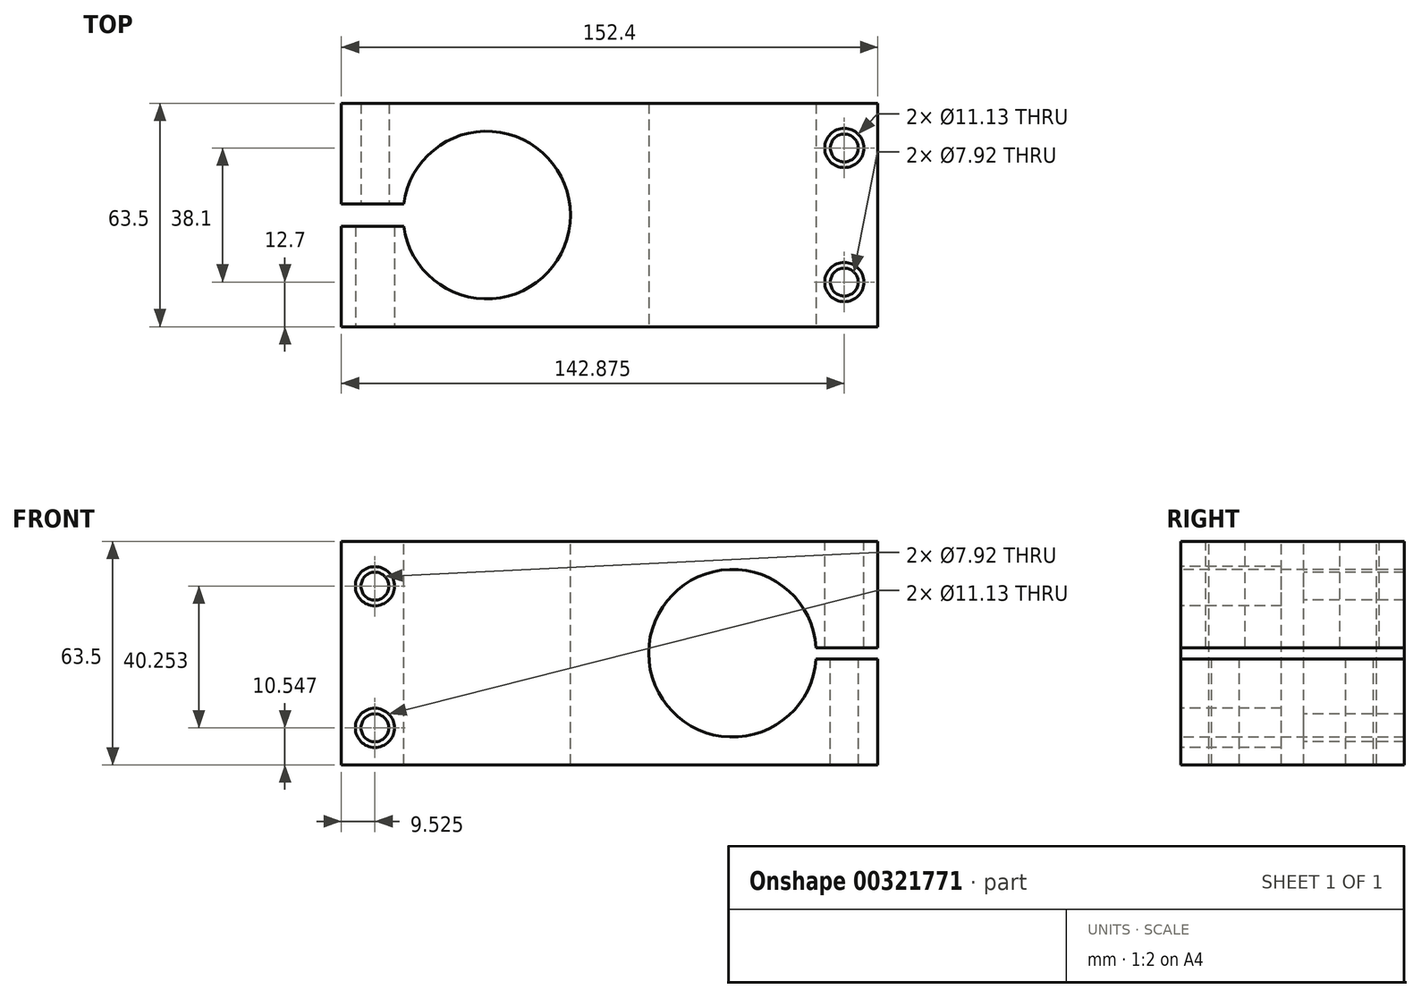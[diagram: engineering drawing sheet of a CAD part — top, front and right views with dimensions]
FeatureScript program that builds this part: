
annotation { "Feature Type Name" : "Feature", "Feature Type Description" : "" }
export const myFeature = defineFeature(function(context is Context, id is Id, definition is map)
    precondition{}
    {
        {
            var Q0;
            Q0=qCreatedBy(makeId("Front.planeOp"),FACE);
            var sketch = newSketch(context, id + "F0", { "sketchPlane" : qUnion([Q0])});
            skLineSegment(sketch, "E0.bottom", {"start": v(-76.2, 31.75) * mm, "end": v(76.2, 31.75) * mm});
            skLineSegment(sketch, "E0.top", {"start": v(-76.2, -31.75) * mm, "end": v(76.2, -31.75) * mm});
            skLineSegment(sketch, "E0.left", {"start": v(-76.2, 31.75) * mm, "end": v(-76.2, -31.75) * mm});
            skLineSegment(sketch, "E0.right", {"start": v(76.2, 31.75) * mm, "end": v(76.2, -31.75) * mm});
            skSolve(sketch);
        }
        {
            var Q0;
            Q0=makeQuery(id+"F0.imprint","IMPRINT",FACE,{"disambiguationData":[TD([[makeQuery(id+"F0.imprint","IMPRINT",EDGE,{"derivedFrom":sQuery(id+"F0.wireOp",EDGE,"E0.bottom")}),-1.0]])]});
            extrude(context, id + "F1", {"entities" : qUnion([Q0]), "endBound" : BoundingType.SYMMETRIC, "depth" : 63.5 * mm});
        }
        {
            var Q0;
            Q0=makeQuery(id+"F1.opExtrude","SWEPT_FACE",FACE,{"disambiguationData":[OSD([sQuery(id+"F0.wireOp",EDGE,"E0.bottom")])]});
            var sketch = newSketch(context, id + "F2", { "sketchPlane" : qUnion([Q0])});
            skPoint(sketch, "E1", {"position": v(-34.92, 0) * mm});
            skSolve(sketch);
        }
        {
            var Q0;
            Q0=sQuery(id+"F2.wireOp",VERTEX,"E1");
            var Q1;
            Q1=makeQuery(id+"F1.opExtrude","SWEPT_BODY",BODY,{"disambiguationData":[OSD([sQuery(id+"F0.wireOp",EDGE,"E0.bottom"),sQuery(id+"F0.wireOp",EDGE,"E0.top"),sQuery(id+"F0.wireOp",EDGE,"E0.left"),sQuery(id+"F0.wireOp",EDGE,"E0.right")])]});
            hole(context, id + "F3", {"style" : HoleStyle.SIMPLE, "endStyle" : HoleEndStyle.THROUGH, "holeDiameter" : 47.62 * mm, "tappedDepth" : 12.7 * mm, "tapClearance" : 3, "locations" : qUnion([Q0]), "scope" : qUnion([Q1])});
        }
        {
            var Q0;
            Q0=makeQuery(id+"F1.opExtrude","CAP_FACE",FACE,{"disambiguationData":[OSD([sQuery(id+"F0.wireOp",EDGE,"E0.bottom"),sQuery(id+"F0.wireOp",EDGE,"E0.top"),sQuery(id+"F0.wireOp",EDGE,"E0.left"),sQuery(id+"F0.wireOp",EDGE,"E0.right")])],"isStart":false});
            var sketch = newSketch(context, id + "F4", { "sketchPlane" : qUnion([Q0])});
            skPoint(sketch, "E2", {"position": v(34.93, 0) * mm});
            skSolve(sketch);
        }
        {
            var Q0;
            Q0=sQuery(id+"F4.wireOp",VERTEX,"E2");
            var Q1;
            Q1=makeQuery(id+"F1.opExtrude","SWEPT_BODY",BODY,{"disambiguationData":[OSD([sQuery(id+"F0.wireOp",EDGE,"E0.bottom"),sQuery(id+"F0.wireOp",EDGE,"E0.top"),sQuery(id+"F0.wireOp",EDGE,"E0.left"),sQuery(id+"F0.wireOp",EDGE,"E0.right")])]});
            hole(context, id + "F5", {"style" : HoleStyle.SIMPLE, "endStyle" : HoleEndStyle.THROUGH, "holeDiameter" : 47.62 * mm, "tappedDepth" : 12.7 * mm, "tapClearance" : 3, "locations" : qUnion([Q0]), "scope" : qUnion([Q1])});
        }
        {
            var Q0;
            Q0=makeQuery(id+"F1.opExtrude","SWEPT_FACE",FACE,{"disambiguationData":[OSD([sQuery(id+"F0.wireOp",EDGE,"E0.bottom")])]});
            var sketch = newSketch(context, id + "F6", { "sketchPlane" : qUnion([Q0])});
            skPoint(sketch, "E3", {"position": v(66.67, 19.05) * mm});
            skSolve(sketch);
        }
        {
            var Q0;
            {var subQ0=sQuery(id+"F0.wireOp",EDGE,"E0.bottom");Q0=makeQuery(id+"F6.imprint","IMPRINT",FACE,{"disambiguationData":[TD([[makeQuery(id+"F6.imprint","IMPRINT",EDGE,{"derivedFrom":makeQuery(id+"F1.opExtrude","CAP_EDGE",EDGE,{"disambiguationData":[OSD([subQ0])],"isStart":true})}),-1.0]])]});}
            var sketch = newSketch(context, id + "F7", { "sketchPlane" : qUnion([Q0])});
            skPoint(sketch, "E4", {"position": v(66.67, -19.05) * mm});
            skSolve(sketch);
        }
        {
            var Q0;
            Q0=makeQuery(id+"F1.opExtrude","CAP_FACE",FACE,{"disambiguationData":[OSD([sQuery(id+"F0.wireOp",EDGE,"E0.bottom"),sQuery(id+"F0.wireOp",EDGE,"E0.top"),sQuery(id+"F0.wireOp",EDGE,"E0.left"),sQuery(id+"F0.wireOp",EDGE,"E0.right")])],"isStart":false});
            var sketch = newSketch(context, id + "F8", { "sketchPlane" : qUnion([Q0])});
            skPoint(sketch, "E5", {"position": v(-66.67, 19.05) * mm});
            skSolve(sketch);
        }
        {
            var Q0;
            Q0=makeQuery(id+"F8.imprint","IMPRINT",FACE,{"disambiguationData":[TD([[makeQuery(id+"F8.imprint","IMPRINT",EDGE,{"derivedFrom":makeQuery(id+"F1.opExtrude","CAP_EDGE",EDGE,{"disambiguationData":[OSD([sQuery(id+"F0.wireOp",EDGE,"E0.bottom")])],"isStart":false})}),-1.0]])]});
            var sketch = newSketch(context, id + "F9", { "sketchPlane" : qUnion([Q0])});
            skPoint(sketch, "E6", {"position": v(-66.67, -21.2) * mm});
            skSolve(sketch);
        }
        {
            var Q0;
            Q0=makeQuery(id+"F1.opExtrude","SWEPT_FACE",FACE,{"disambiguationData":[OSD([sQuery(id+"F0.wireOp",EDGE,"E0.right")])]});
            var sketch = newSketch(context, id + "F10", { "sketchPlane" : qUnion([Q0])});
            skLineSegment(sketch, "E7.bottom", {"start": v(-31.75, 1.59) * mm, "end": v(31.75, 1.59) * mm});
            skLineSegment(sketch, "E7.top", {"start": v(-31.75, -1.59) * mm, "end": v(31.75, -1.59) * mm});
            skLineSegment(sketch, "E7.left", {"start": v(-31.75, 1.59) * mm, "end": v(-31.75, -1.59) * mm});
            skLineSegment(sketch, "E7.right", {"start": v(31.75, 1.59) * mm, "end": v(31.75, -1.59) * mm});
            skSolve(sketch);
        }
        {
            var Q0;
            Q0=makeQuery(id+"F10.imprint","IMPRINT",FACE,{"disambiguationData":[TD([[makeQuery(id+"F10.imprint","IMPRINT",EDGE,{"derivedFrom":sQuery(id+"F10.wireOp",EDGE,"E7.bottom")}),-1.0]])]});
            extrude(context, id + "F11", {"entities" : qUnion([Q0]), "operationType" : NewBodyOperationType.REMOVE, "endBound" : BoundingType.SYMMETRIC, "oppositeDirection" : true, "depth" : 38.1 * mm});
        }
        {
            var Q0;
            Q0=sQuery(id+"F6.wireOp",VERTEX,"E3");
            var Q1;
            Q1=sQuery(id+"F7.wireOp",VERTEX,"E4");
            var Q2;
            Q2=sQuery(id+"F8.wireOp",VERTEX,"E5");
            var Q3;
            Q3=sQuery(id+"F9.wireOp",VERTEX,"E6");
            var Q4;
            Q4=makeQuery(id+"F1.opExtrude","SWEPT_BODY",BODY,{"disambiguationData":[OSD([sQuery(id+"F0.wireOp",EDGE,"E0.bottom"),sQuery(id+"F0.wireOp",EDGE,"E0.top"),sQuery(id+"F0.wireOp",EDGE,"E0.left"),sQuery(id+"F0.wireOp",EDGE,"E0.right")])]});
            hole(context, id + "F12", {"style" : HoleStyle.C_BORE, "endStyle" : HoleEndStyle.THROUGH, "holeDiameter" : 7.92 * mm, "cBoreDiameter" : 11.13 * mm, "cBoreDepth" : 31.75 * mm, "tappedDepth" : 12.7 * mm, "tapClearance" : 3, "locations" : qUnion([Q0, Q1, Q2, Q3]), "scope" : qUnion([Q4])});
        }
        {
            var Q0;
            Q0=makeQuery(id+"F1.opExtrude","SWEPT_FACE",FACE,{"disambiguationData":[OSD([sQuery(id+"F0.wireOp",EDGE,"E0.left")])]});
            var sketch = newSketch(context, id + "F13", { "sketchPlane" : qUnion([Q0])});
            skLineSegment(sketch, "E8.bottom", {"start": v(-3.17, -31.75) * mm, "end": v(3.18, -31.75) * mm});
            skLineSegment(sketch, "E8.top", {"start": v(-3.18, 31.75) * mm, "end": v(3.17, 31.75) * mm});
            skLineSegment(sketch, "E8.left", {"start": v(-3.17, -31.75) * mm, "end": v(-3.18, 31.75) * mm});
            skLineSegment(sketch, "E8.right", {"start": v(3.18, -31.75) * mm, "end": v(3.17, 31.75) * mm});
            skSolve(sketch);
        }
        {
            var Q0;
            Q0=makeQuery(id+"F13.imprint","IMPRINT",FACE,{"disambiguationData":[TD([[makeQuery(id+"F13.imprint","IMPRINT",EDGE,{"derivedFrom":sQuery(id+"F13.wireOp",EDGE,"E8.bottom")}),-1.0]])]});
            extrude(context, id + "F14", {"entities" : qUnion([Q0]), "operationType" : NewBodyOperationType.REMOVE, "oppositeDirection" : true, "depth" : 50.8 * mm});
        }
    });
